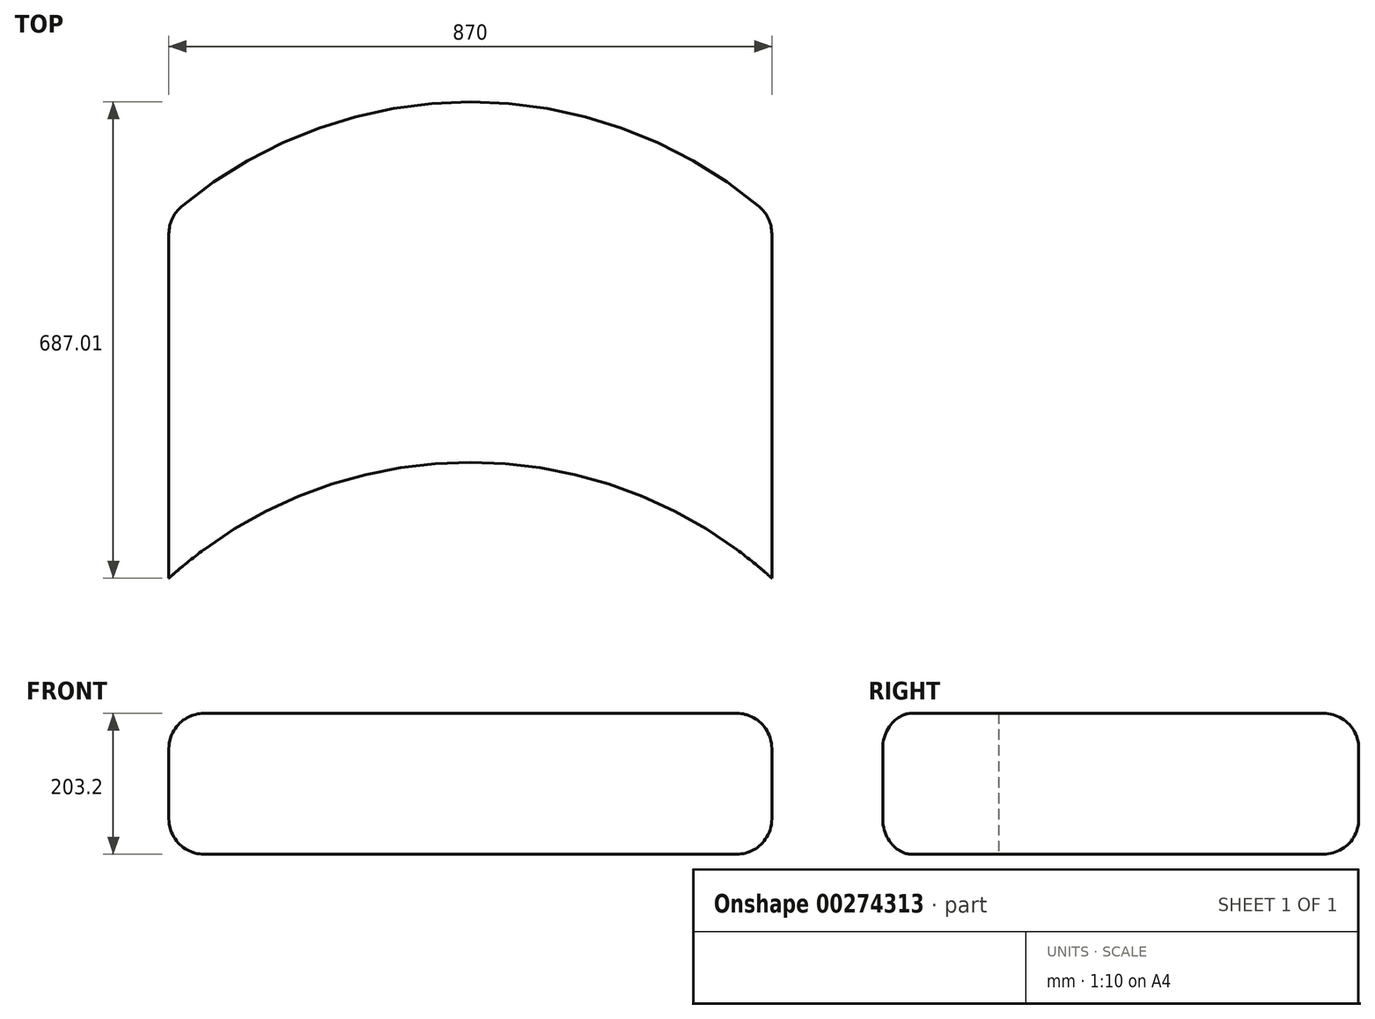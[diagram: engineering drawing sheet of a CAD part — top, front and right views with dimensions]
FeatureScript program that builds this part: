
annotation { "Feature Type Name" : "Feature", "Feature Type Description" : "" }
export const myFeature = defineFeature(function(context is Context, id is Id, definition is map)
    precondition{}
    {
        {
            var Q0;
            Q0=qCreatedBy(makeId("Top.planeOp"),FACE);
            var sketch = newSketch(context, id + "F0", { "sketchPlane" : qUnion([Q0])});
            skLineSegment(sketch, "E0", {"start": v(0, 0) * mm, "end": v(-435, 0) * mm});
            skLineSegment(sketch, "E1", {"start": v(0, 0) * mm, "end": v(435, 0) * mm});
            skLineSegment(sketch, "E2", {"start": v(-435, 0) * mm, "end": v(-435, 520) * mm});
            skLineSegment(sketch, "E3", {"start": v(435, 0) * mm, "end": v(435, 520) * mm});
            skArc(sketch, "E4", {"start": v(435, 520) * mm, "mid": v(0, 687.01) * mm, "end": v(-435, 520) * mm});
            skArc(sketch, "E5", {"start": v(435, 0) * mm, "mid": v(0, 167.01) * mm, "end": v(-435, 0) * mm});
            skSolve(sketch);
        }
        {
            var Q0;
            Q0=makeQuery(id+"F0.imprint","IMPRINT",FACE,{"disambiguationData":[TD([[makeQuery(id+"F0.imprint","IMPRINT",EDGE,{"derivedFrom":sQuery(id+"F0.wireOp",EDGE,"E2")}),-1.0]])]});
            extrude(context, id + "F1", {"entities" : qUnion([Q0]), "depth" : 203.2 * mm});
        }
        {
            var Q0;
            Q0=makeQuery(id+"F1.opExtrude","CAP_EDGE",EDGE,{"disambiguationData":[OSD([sQuery(id+"F0.wireOp",EDGE,"E4")])],"isStart":false});
            var Q1;
            Q1=makeQuery(id+"F1.opExtrude","SWEPT_EDGE",EDGE,{"disambiguationData":[OSD([sQuery(id+"F0.wireOp",EDGE,"E2"),sQuery(id+"F0.wireOp",EDGE,"E4")])]});
            var Q2;
            Q2=makeQuery(id+"F1.opExtrude","CAP_EDGE",EDGE,{"disambiguationData":[OSD([sQuery(id+"F0.wireOp",EDGE,"E4")])],"isStart":true});
            var Q3;
            Q3=makeQuery(id+"F1.opExtrude","SWEPT_FACE",FACE,{"disambiguationData":[OSD([sQuery(id+"F0.wireOp",EDGE,"E4")])]});
            var Q4;
            Q4=makeQuery(id+"F1.opExtrude","CAP_EDGE",EDGE,{"disambiguationData":[OSD([sQuery(id+"F0.wireOp",EDGE,"E3")])],"isStart":true});
            var Q5;
            Q5=makeQuery(id+"F1.opExtrude","CAP_EDGE",EDGE,{"disambiguationData":[OSD([sQuery(id+"F0.wireOp",EDGE,"E3")])],"isStart":false});
            var Q6;
            Q6=makeQuery(id+"F1.opExtrude","CAP_EDGE",EDGE,{"disambiguationData":[OSD([sQuery(id+"F0.wireOp",EDGE,"E2")])],"isStart":false});
            var Q7;
            Q7=makeQuery(id+"F1.opExtrude","CAP_EDGE",EDGE,{"disambiguationData":[OSD([sQuery(id+"F0.wireOp",EDGE,"E2")])],"isStart":true});
            fillet(context, id + "F2", {"entities" : qUnion([Q0, Q1, Q2, Q3, Q4, Q5, Q6, Q7]), "radius" : 50.8 * mm, "tangentPropagation" : true, "allowEdgeOverflow" : false});
        }
    });
